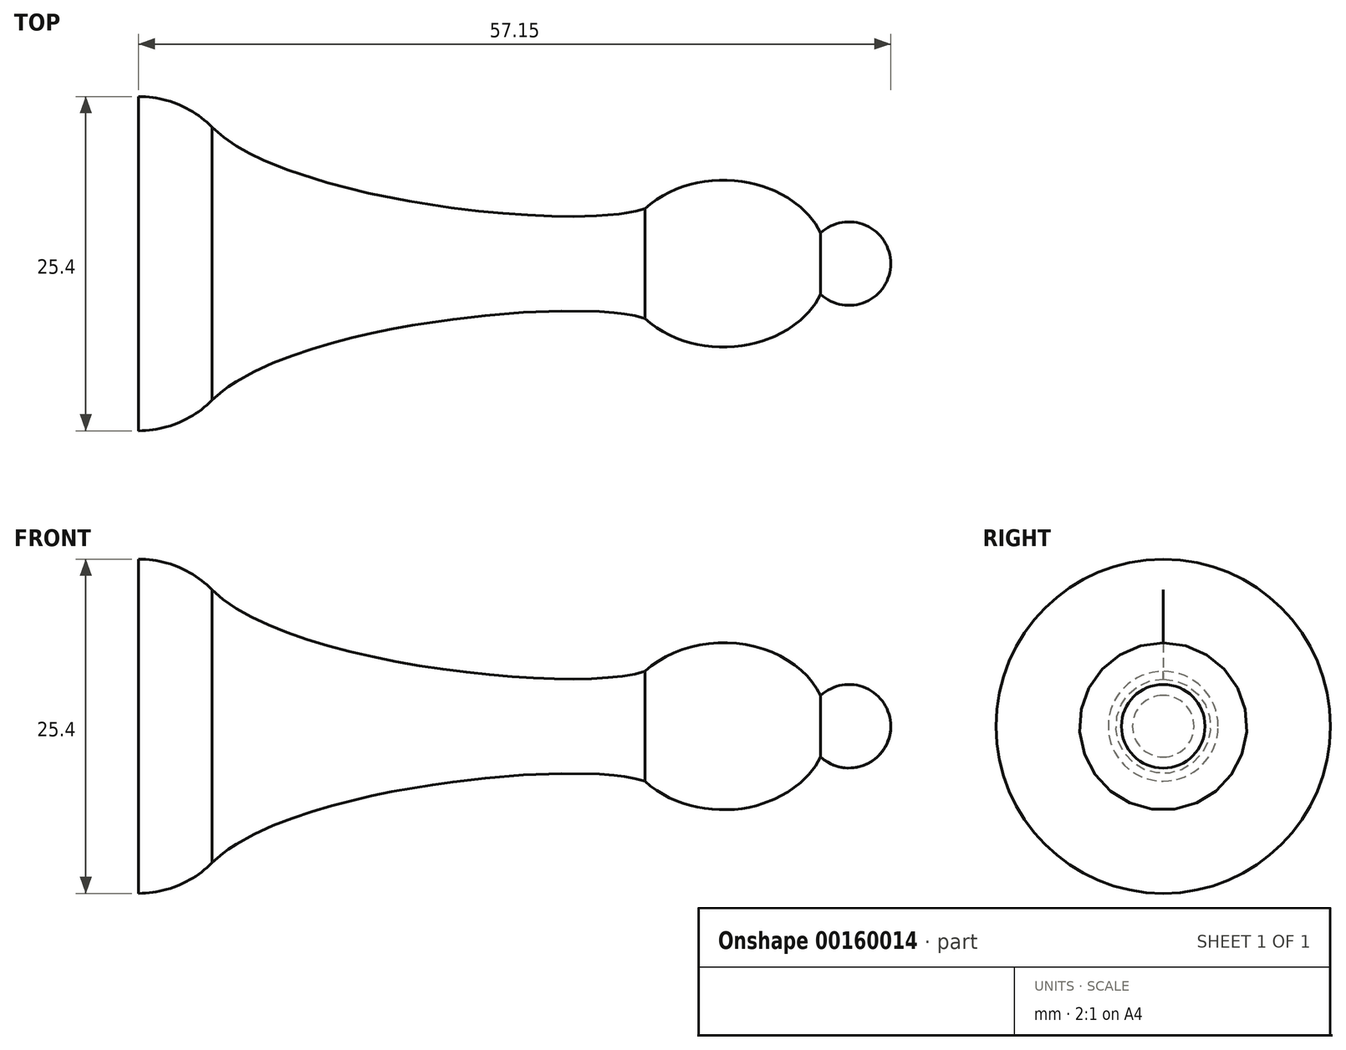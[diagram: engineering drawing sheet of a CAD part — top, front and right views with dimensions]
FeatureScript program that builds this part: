
annotation { "Feature Type Name" : "Feature", "Feature Type Description" : "" }
export const myFeature = defineFeature(function(context is Context, id is Id, definition is map)
    precondition{}
    {
        {
            var Q0;
            Q0=qCreatedBy(makeId("Front.planeOp"),FACE);
            var sketch = newSketch(context, id + "F0", { "sketchPlane" : qUnion([Q0])});
            skLineSegment(sketch, "E0", {"start": v(0, 0) * mm, "end": v(0, 12.7) * mm});
            skLineSegment(sketch, "E1", {"start": v(0, 12.7) * mm, "end": v(0, 12.7) * mm});
            skEllipticalArc(sketch, "E2", {});
            skFitSpline(sketch, "E3", {"points": [v(4.3, 12.7) * mm, v(38.47, 4.17) * mm], "startDerivative": vector(3.5, -22.34) * mm, "endDerivative": vector(17.34, 5.92) * mm});
            skArc(sketch, "E4.filletArc", {"start": v(5.6, 10.37) * mm, "mid": v(3.03, 12.1) * mm, "end": v(0, 12.7) * mm});
            skPoint(sketch, "E5", {"position": v(53.98, 0) * mm});
            skArc(sketch, "E6", {"start": v(57.15, 0) * mm, "mid": v(55.25, 2.9) * mm, "end": v(51.83, 2.34) * mm});
            skLineSegment(sketch, "E7", {"start": v(0, 0) * mm, "end": v(57.15, 0) * mm});
            const initialGuessF0  = {"E2": [0.04445, 0, 1, 0, 0.007937494111257527, 0.006349995289006024, 0.3773819723101745, 2.4243456330156365]};
            skSetInitialGuess(sketch, initialGuessF0);
            skSolve(sketch);
        }
        {
            var Q0;
            Q0=makeQuery(id+"F0.imprint","IMPRINT",FACE,{"disambiguationData":[TD([[makeQuery(id+"F0.imprint","IMPRINT",EDGE,{"derivedFrom":sQuery(id+"F0.wireOp",EDGE,"E0")}),-1.0]])]});
            var Q1;
            Q1=sQuery(id+"F0.wireOp",EDGE,"E7");
            revolve(context, id + "F1", {"entities" : qUnion([Q0]), "axis" : qUnion([Q1]), "revolveType" : RevolveType.FULL});
        }
    });
